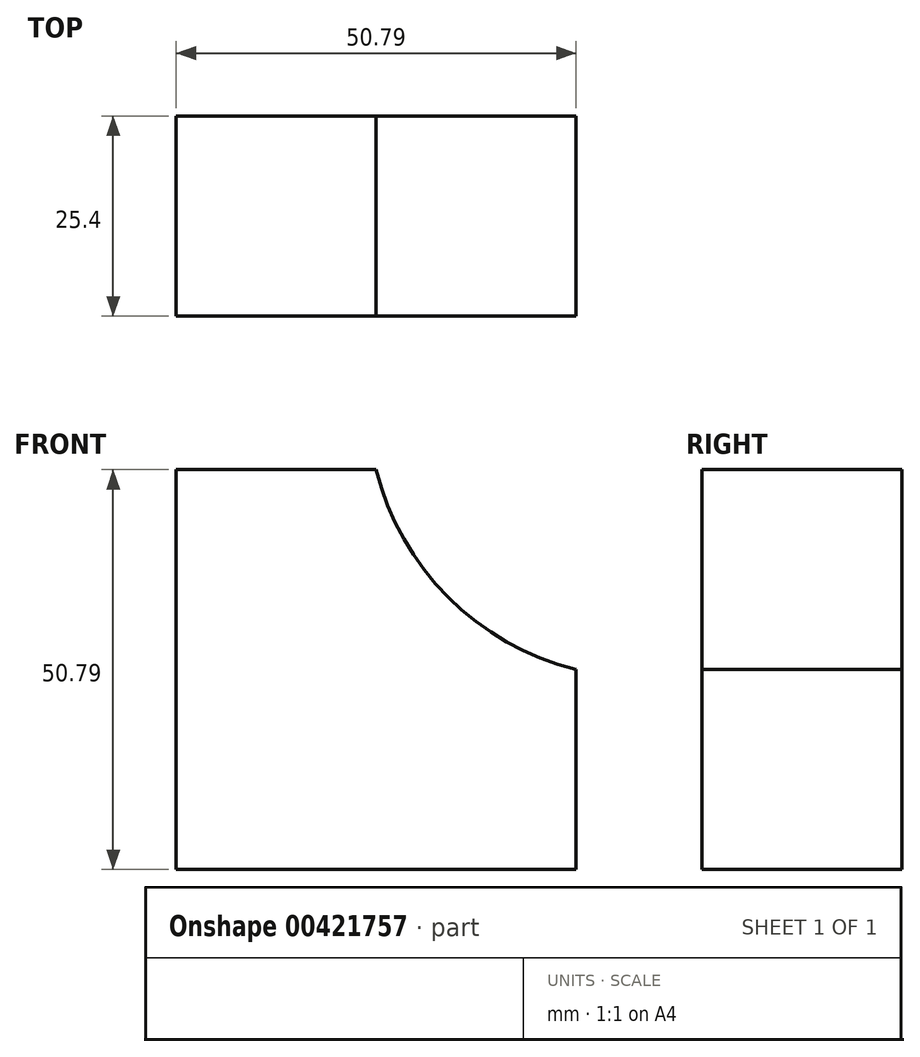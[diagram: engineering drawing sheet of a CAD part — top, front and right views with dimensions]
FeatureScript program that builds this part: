
annotation { "Feature Type Name" : "Feature", "Feature Type Description" : "" }
export const myFeature = defineFeature(function(context is Context, id is Id, definition is map)
    precondition{}
    {
        {
            var Q0;
            Q0=qCreatedBy(makeId("Front.planeOp"),FACE);
            var sketch = newSketch(context, id + "F0", { "sketchPlane" : qUnion([Q0])});
            skLineSegment(sketch, "E0", {"start": v(0, 0) * mm, "end": v(-50.8, 0) * mm});
            skLineSegment(sketch, "E1", {"start": v(-50.8, 0) * mm, "end": v(-50.8, 50.8) * mm});
            skLineSegment(sketch, "E2", {"start": v(-50.8, 50.8) * mm, "end": v(-25.4, 50.8) * mm});
            skLineSegment(sketch, "E3", {"start": v(0, 25.4) * mm, "end": v(0, 0) * mm});
            skArc(sketch, "E4", {"start": v(-25.4, 50.8) * mm, "mid": v(-16.23, 34.56) * mm, "end": v(0, 25.4) * mm});
            skSolve(sketch);
        }
        {
            var Q0;
            Q0=makeQuery(id+"F0.imprint","IMPRINT",FACE,{"disambiguationData":[TD([[makeQuery(id+"F0.imprint","IMPRINT",EDGE,{"derivedFrom":sQuery(id+"F0.wireOp",EDGE,"E0")}),-1.0]])]});
            extrude(context, id + "F1", {"entities" : qUnion([Q0]), "depth" : 25.4 * mm});
        }
    });
